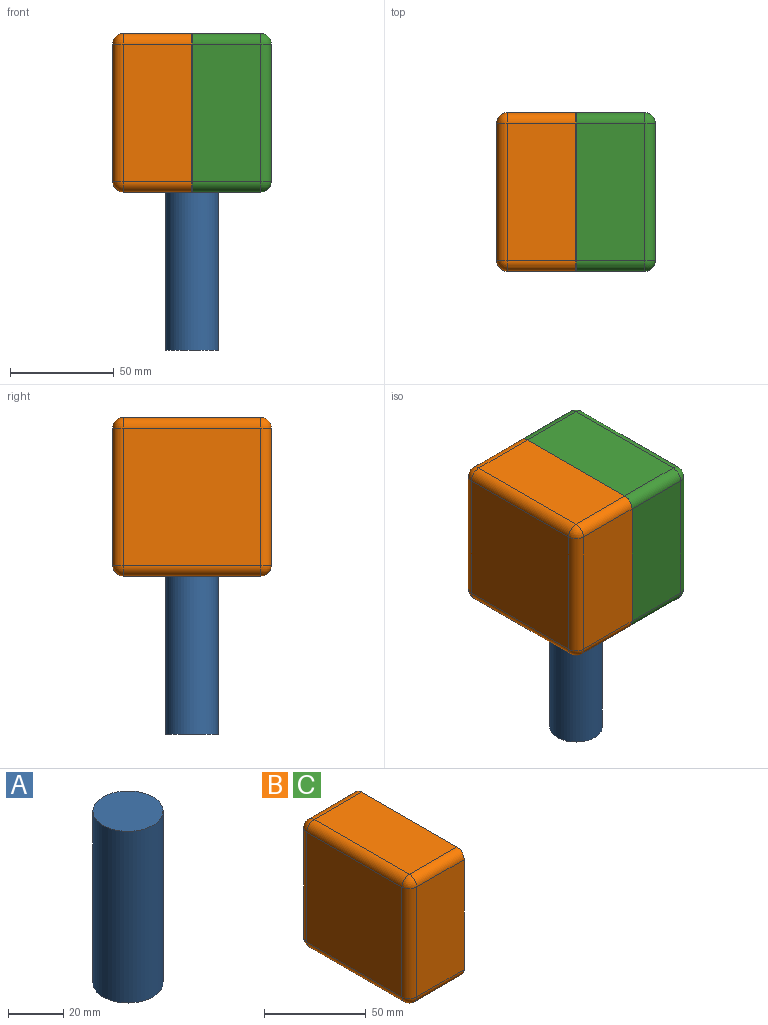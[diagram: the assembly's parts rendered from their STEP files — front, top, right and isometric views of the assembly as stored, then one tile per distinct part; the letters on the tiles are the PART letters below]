
ASSEMBLY  parts=3 mates=6
PART A: 3 faces, bbox 25.4x25.4x76.2 mm
  f0: plane 25.4x25.4mm, normal (0,0,-1), area 506.7mm2, adj f2
  f1: plane 25.4x25.4mm, normal (0,0,1), area 506.7mm2, adj f2
  f2: cylinder r=12.7mm len=76.2mm, axis (0,0,1), area 6080.5mm2, adj f0,f1
PART B: 23 faces, bbox 38.1x76.2x76.2 mm
  f0: plane 76.2x76.2mm, normal (1,0,0), area 726.2mm2, adj f1,f2,f4,f5,f6,f7,f9,f10
  f1: plane 66.04x33.02mm, normal (0,0,-1), area 2180.6mm2, adj f0,f11,f12,f13
  f2: plane 66.04x33.02mm, normal (0,0,1), area 2180.6mm2, adj f0,f16,f19,f22
  f3: plane 66.04x66.04mm, normal (-1,0,0), area 4361.3mm2, adj f12,f17,f18,f22
  f4: plane 66.04x33.02mm, normal (0,-1,0), area 2180.6mm2, adj f0,f11,f16,f17
  f5: plane 66.04x33.02mm, normal (0,1,0), area 2180.6mm2, adj f0,f13,f18,f19
  f6: plane 71.12x35.56mm, normal (0,0,1), area 2529mm2, adj f0,f8,f9,f10
  f7: plane 71.12x35.56mm, normal (0,0,-1), area 2529mm2, adj f0,f8,f9,f10
  f8: plane 71.12x71.12mm, normal (1,0,0), area 5058.1mm2, adj f6,f7,f9,f10
  f9: plane 71.12x35.56mm, normal (0,1,0), area 2529mm2, adj f0,f6,f7,f8
  f10: plane 71.12x35.56mm, normal (0,-1,0), area 2529mm2, adj f0,f6,f7,f8
  f11: cylinder r=5.08mm len=33.02mm, axis (-1,0,0), area 263.5mm2, adj f0,f1,f4,f14
  f12: cylinder r=5.08mm len=66.04mm, axis (0,1,0), area 527mm2, adj f1,f3,f14,f15
  f13: cylinder r=5.08mm len=33.02mm, axis (1,0,0), area 263.5mm2, adj f0,f1,f5,f15
  f14: sphere r=5.08mm, area 40.5mm2, adj f11,f12,f17
  f15: sphere r=5.08mm, area 40.5mm2, adj f12,f13,f18
  f16: cylinder r=5.08mm len=33.02mm, axis (1,0,0), area 263.5mm2, adj f0,f2,f4,f20
  f17: cylinder r=5.08mm len=66.04mm, axis (0,0,1), area 527mm2, adj f3,f4,f14,f20
  f18: cylinder r=5.08mm len=66.04mm, axis (0,0,-1), area 527mm2, adj f3,f5,f15,f21
  f19: cylinder r=5.08mm len=33.02mm, axis (-1,0,0), area 263.5mm2, adj f0,f2,f5,f21
  f20: sphere r=5.08mm, area 40.5mm2, adj f16,f17,f22
  f21: sphere r=5.08mm, area 40.5mm2, adj f18,f19,f22
  f22: cylinder r=5.08mm len=66.04mm, axis (0,1,0), area 527mm2, adj f2,f3,f20,f21
PART C: same geometry as B
PLACE A t=(4.6,-54.04,-155.27)mm
PLACE B t=(-20.8,-15.94,-79.07)mm
PLACE C rot(axis=(0,0,1),180deg) t=(55.4,-92.14,-79.07)mm
MATE planar C.f4 <-> B.f5  axis (0,1,0) through (33.81,-15.94,-40.97)mm
MATE planar A.f2 <-> C.f1  axis (0,0,1) through (17.3,-54.04,-79.07)mm
MATE fastened C.f1 <-> A.f2  axis (0,0,-1) through (17.3,-54.04,-79.07)mm
MATE planar C.f2 <-> B.f2  axis (0,0,1) through (33.81,-54.04,-2.87)mm
MATE planar C.f1 <-> A.f2  axis (0,0,-1) through (33.81,-54.04,-79.07)mm
MATE planar B.f0 <-> C.f0  axis (1,0,0) through (17.3,-54.04,-40.97)mm
